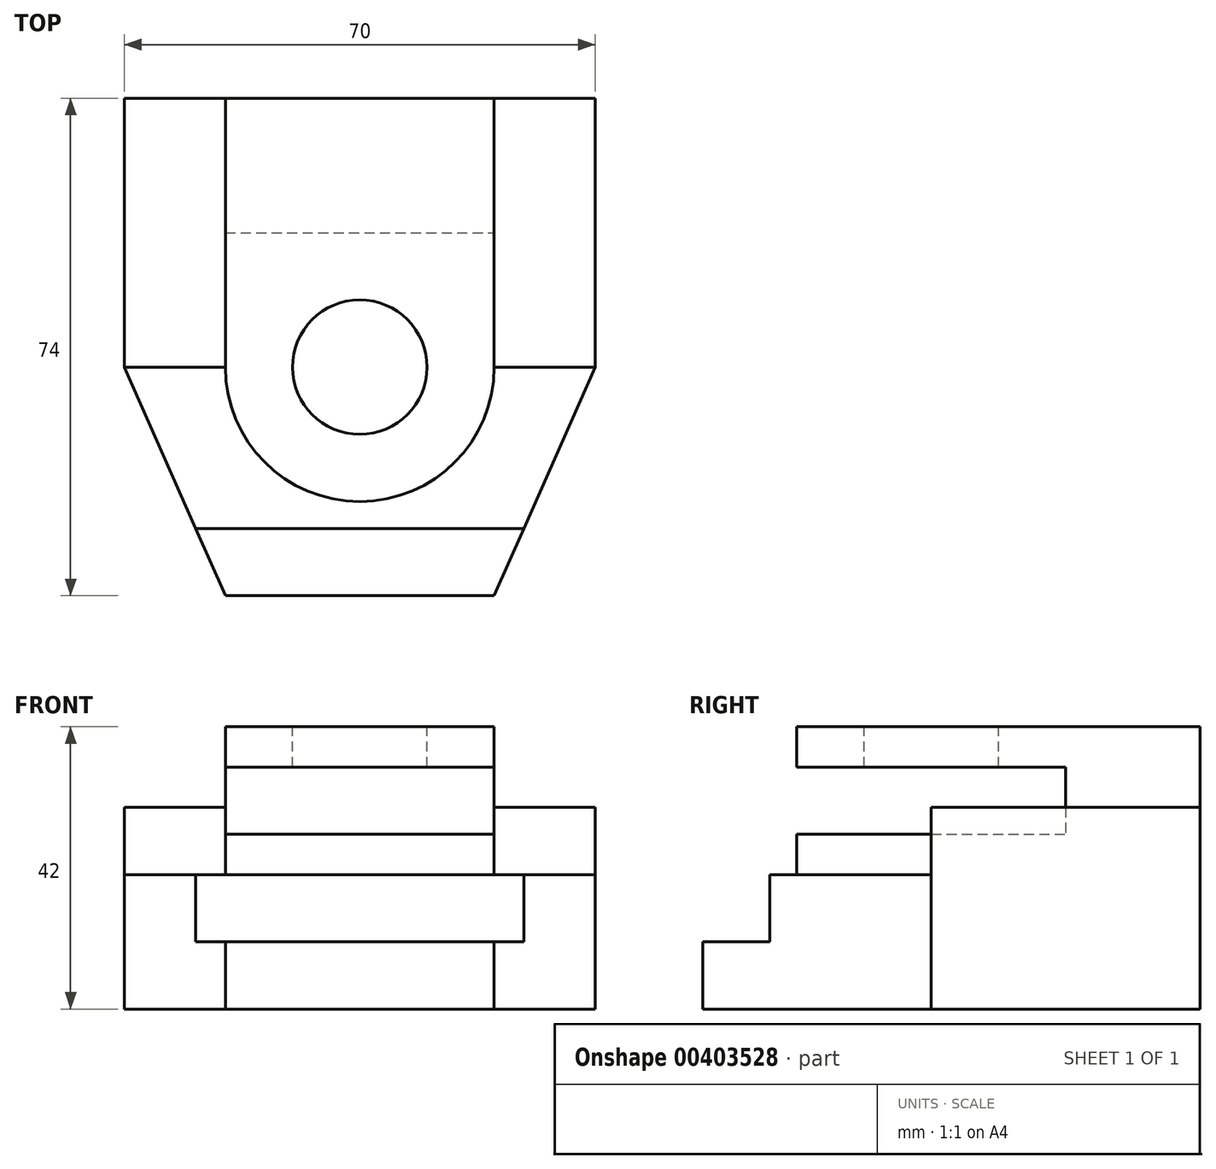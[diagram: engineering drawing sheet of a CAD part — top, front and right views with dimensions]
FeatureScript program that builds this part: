
annotation { "Feature Type Name" : "Feature", "Feature Type Description" : "" }
export const myFeature = defineFeature(function(context is Context, id is Id, definition is map)
    precondition{}
    {
        {
            var Q0;
            Q0=qCreatedBy(makeId("Top.planeOp"),FACE);
            var sketch = newSketch(context, id + "F0", { "sketchPlane" : qUnion([Q0])});
            skLineSegment(sketch, "E0", {"start": v(0, 18.6) * mm, "end": v(40, 18.6) * mm});
            skLineSegment(sketch, "E1", {"start": v(40, 18.6) * mm, "end": v(40, -21.4) * mm});
            skLineSegment(sketch, "E2", {"start": v(0, 18.6) * mm, "end": v(0, -21.4) * mm});
            skArc(sketch, "E3", {"start": v(0, -21.4) * mm, "mid": v(20, -41.4) * mm, "end": v(40, -21.4) * mm});
            skSolve(sketch);
        }
        {
            var Q0;
            Q0 = qSketchRegion(id + "F0", true);
            extrude(context, id + "F1", {"entities" : qUnion([Q0]), "depth" : 22 * mm});
        }
        {
            var Q0;
            Q0=makeQuery(id+"F1.opExtrude","SWEPT_FACE",FACE,{"disambiguationData":[OSD([sQuery(id+"F0.wireOp",EDGE,"E1")])]});
            var sketch = newSketch(context, id + "F2", { "sketchPlane" : qUnion([Q0])});
            skLineSegment(sketch, "E4.bottom", {"start": v(-1.4, 6) * mm, "end": v(-41.4, 6) * mm});
            skLineSegment(sketch, "E4.top", {"start": v(-1.4, 16) * mm, "end": v(-41.4, 16) * mm});
            skLineSegment(sketch, "E4.left", {"start": v(-1.4, 6) * mm, "end": v(-1.4, 16) * mm});
            skLineSegment(sketch, "E4.right", {"start": v(-41.4, 6) * mm, "end": v(-41.4, 16) * mm});
            skSolve(sketch);
        }
        {
            var Q0;
            Q0=makeQuery(id+"F1.opExtrude","CAP_FACE",FACE,{"disambiguationData":[OSD([sQuery(id+"F0.wireOp",EDGE,"E0"),sQuery(id+"F0.wireOp",EDGE,"E1"),sQuery(id+"F0.wireOp",EDGE,"E2"),sQuery(id+"F0.wireOp",EDGE,"E3")])],"isStart":false});
            var sketch = newSketch(context, id + "F3", { "sketchPlane" : qUnion([Q0])});
            skCircle(sketch, "E5", {"center": v(20, -21.4) * mm, "radius": 10 * mm});
            skPoint(sketch, "E5.centerSnap0", {"position": v(20, -41.4) * mm});
            skSolve(sketch);
        }
        {
            var Q0;
            Q0 = qSketchRegion(id + "F3", true);
            extrude(context, id + "F4", {"entities" : qUnion([Q0]), "operationType" : NewBodyOperationType.REMOVE, "oppositeDirection" : true, "depth" : 6 * mm});
        }
        {
            var Q0;
            Q0=makeQuery(id+"F1.opExtrude","CAP_FACE",FACE,{"disambiguationData":[OSD([sQuery(id+"F0.wireOp",EDGE,"E0"),sQuery(id+"F0.wireOp",EDGE,"E1"),sQuery(id+"F0.wireOp",EDGE,"E2"),sQuery(id+"F0.wireOp",EDGE,"E3")])],"isStart":true});
            var sketch = newSketch(context, id + "F5", { "sketchPlane" : qUnion([Q0])});
            skLineSegment(sketch, "E6", {"start": v(-15, 21.4) * mm, "end": v(55, 21.4) * mm});
            skLineSegment(sketch, "E7", {"start": v(55, 21.4) * mm, "end": v(40, 55.4) * mm});
            skLineSegment(sketch, "E8", {"start": v(40, 55.4) * mm, "end": v(0, 55.4) * mm});
            skLineSegment(sketch, "E9", {"start": v(0, 55.4) * mm, "end": v(-15, 21.4) * mm});
            skLineSegment(sketch, "E10", {"start": v(20, -18.6) * mm, "end": v(20, 41.4) * mm, "construction": true});
            skSolve(sketch);
        }
        {
            var Q0;
            Q0 = qSketchRegion(id + "F5", true);
            extrude(context, id + "F6", {"entities" : qUnion([Q0]), "operationType" : NewBodyOperationType.ADD, "depth" : 20 * mm});
        }
        {
            var Q0;
            Q0=makeQuery(id+"F1.opExtrude","SWEPT_FACE",FACE,{"disambiguationData":[OSD([sQuery(id+"F0.wireOp",EDGE,"E1")])]});
            var sketch = newSketch(context, id + "F7", { "sketchPlane" : qUnion([Q0])});
            skLineSegment(sketch, "E11.bottom", {"start": v(-55.4, 0) * mm, "end": v(-45.4, 0) * mm});
            skLineSegment(sketch, "E11.top", {"start": v(-55.4, -10) * mm, "end": v(-45.4, -10) * mm});
            skLineSegment(sketch, "E11.left", {"start": v(-55.4, 0) * mm, "end": v(-55.4, -10) * mm});
            skLineSegment(sketch, "E11.right", {"start": v(-45.4, 0) * mm, "end": v(-45.4, -10) * mm});
            skSolve(sketch);
        }
        {
            var Q0;
            Q0 = qSketchRegion(id + "F7", true);
            extrude(context, id + "F8", {"entities" : qUnion([Q0]), "operationType" : NewBodyOperationType.REMOVE, "endBound" : BoundingType.THROUGH_ALL, "oppositeDirection" : true, "depth" : 25 * mm, "hasSecondDirection" : true, "secondDirectionBound" : SecondDirectionBoundingType.THROUGH_ALL, "secondDirectionOppositeDirection" : false, "secondDirectionDepth" : 25 * mm});
        }
        {
            var Q0;
            Q0=makeQuery(id+"F1.opExtrude","SWEPT_FACE",FACE,{"disambiguationData":[OSD([sQuery(id+"F0.wireOp",EDGE,"E1")])]});
            var sketch = newSketch(context, id + "F9", { "sketchPlane" : qUnion([Q0])});
            skLineSegment(sketch, "E12.bottom", {"start": v(18.6, 10) * mm, "end": v(-21.4, 10) * mm});
            skLineSegment(sketch, "E12.top", {"start": v(18.6, -20) * mm, "end": v(-21.4, -20) * mm});
            skLineSegment(sketch, "E12.left", {"start": v(18.6, 10) * mm, "end": v(18.6, -20) * mm});
            skLineSegment(sketch, "E12.right", {"start": v(-21.4, 10) * mm, "end": v(-21.4, -20) * mm});
            skSolve(sketch);
        }
        {
            var Q0;
            Q0 = qSketchRegion(id + "F9", true);
            var Q1;
            Q1=makeQuery(id+"F6.opExtrude","SWEPT_FACE",FACE,{"disambiguationData":[OSD([sQuery(id+"F5.wireOp",EDGE,"E7")])]});
            var Q2;
            Q2=makeQuery(id+"F6.opExtrude","CAP_VERTEX",VERTEX,{"disambiguationData":[OSD([sQuery(id+"F5.wireOp",EDGE,"E6"),sQuery(id+"F5.wireOp",EDGE,"E7")])],"isStart":false});
            var Q3;
            Q3=makeQuery(id+"F6.opExtrude","CAP_VERTEX",VERTEX,{"disambiguationData":[OSD([sQuery(id+"F5.wireOp",EDGE,"E6"),sQuery(id+"F5.wireOp",EDGE,"E9")])],"isStart":false});
            extrude(context, id + "F10", {"entities" : qUnion([Q0]), "operationType" : NewBodyOperationType.ADD, "endBound" : BoundingType.UP_TO_VERTEX, "endBoundEntityFace" : qUnion([Q1]), "endBoundEntityVertex" : qUnion([Q2]), "depth" : 25 * mm, "hasSecondDirection" : true, "secondDirectionBound" : SecondDirectionBoundingType.UP_TO_VERTEX, "secondDirectionOppositeDirection" : true, "secondDirectionBoundEntityVertex" : qUnion([Q3]), "secondDirectionDepth" : 25 * mm});
        }
        {
            var Q0;
            Q0 = qSketchRegion(id + "F2", true);
            var Q1;
            Q1=makeQuery(id+"F1.opExtrude","SWEPT_FACE",FACE,{"disambiguationData":[OSD([sQuery(id+"F0.wireOp",EDGE,"E2")])]});
            extrude(context, id + "F11", {"entities" : qUnion([Q0]), "operationType" : NewBodyOperationType.REMOVE, "endBound" : BoundingType.UP_TO_SURFACE, "oppositeDirection" : true, "endBoundEntityFace" : qUnion([Q1]), "depth" : 25 * mm});
        }
    });
